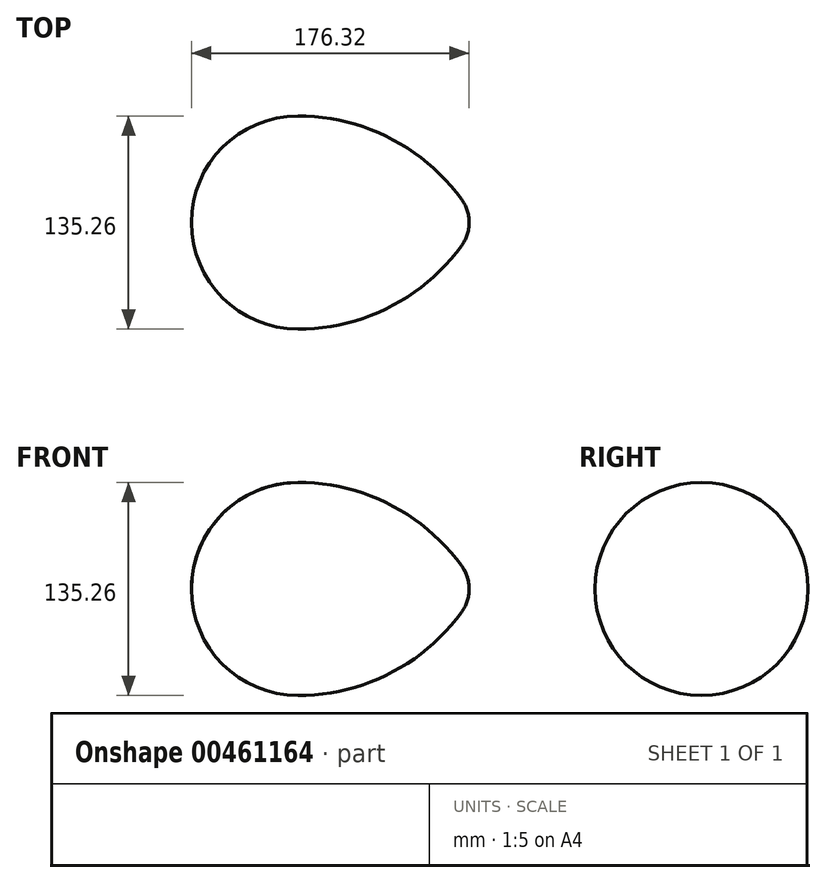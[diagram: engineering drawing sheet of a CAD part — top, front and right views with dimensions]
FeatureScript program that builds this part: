
annotation { "Feature Type Name" : "Feature", "Feature Type Description" : "" }
export const myFeature = defineFeature(function(context is Context, id is Id, definition is map)
    precondition{}
    {
        {
            var Q0;
            Q0=qCreatedBy(makeId("Front.planeOp"),FACE);
            var sketch = newSketch(context, id + "F0", { "sketchPlane" : qUnion([Q0])});
            skLineSegment(sketch, "E0", {"start": v(0, 67.63) * mm, "end": v(0, 42.23) * mm, "construction": true});
            skLineSegment(sketch, "E1", {"start": v(0, -67.63) * mm, "end": v(0, -42.23) * mm, "construction": true});
            skLineSegment(sketch, "E2", {"start": v(0, 42.23) * mm, "end": v(83.3, 0) * mm, "construction": true});
            skLineSegment(sketch, "E3", {"start": v(41.65, 21.12) * mm, "end": v(0, -61.02) * mm, "construction": true});
            skArc(sketch, "E4", {"start": v(103.78, 15.01) * mm, "mid": v(58.18, 53.72) * mm, "end": v(0, 67.63) * mm});
            skLineSegment(sketch, "E5", {"start": v(-67.63, 0) * mm, "end": v(113.26, 0) * mm});
            skPoint(sketch, "E6.orphan", {"position": v(-84.4, 0) * mm});
            skArc(sketch, "E7.trimOffspring", {"start": v(108.7, 0) * mm, "mid": v(107.43, 7.9) * mm, "end": v(103.78, 15.01) * mm});
            skArc(sketch, "E8.trimOffspring", {"start": v(0, 67.63) * mm, "mid": v(-47.82, 47.82) * mm, "end": v(-67.63, 0) * mm});
            skSolve(sketch);
        }
        {
            var Q0;
            Q0=qSketchRegion(id+"F0",true);
            var Q1;
            Q1=sQuery(id+"F0.wireOp",EDGE,"E5");
            revolve(context, id + "F1", {"entities" : qUnion([Q0]), "axis" : qUnion([Q1]), "revolveType" : RevolveType.FULL});
        }
    });
